# Revit family: PC RCD
name_source: partatom
category: Attrezzature speciali
revit_build: Autodesk Revit 2016 (Build: 20150714_1515(x64)
units: mm (PartAtom-declared; Revit-internal decimal feet)

## family parameters
Basato su piano di lavoro = No
Condiviso = No
Punto di calcolo locali = No
Quota connettore circolare = Usa diametro
Sempre verticale = Sì
Taglio con vuoti quando caricato = No
Tipo di parte = Normale

## types (6) — shared parameters
230 Volt = No
400 Volt = Sì
Air gap = Sì
Capacity factor = 80.00%
Clearance = 430 mm
Electrical supply = 400 V
Height = 1460 mm  [stored 4.79003 ft]
Latent Heat = 3.12 kW
Length = 717 mm  [stored 2.35236 ft]
Output racks/h = 40
Overall size = 1970 mm  [stored 6.46325 ft]
Rack size = 500 x 500
Rinse water consumption = 2.5 L
Sensible Heat = 2.15 kW
Tank drain = 35 mm  [stored 0.114829 ft]
Water inlet = 1"
Width = 740 mm  [stored 2.42782 ft]

## per-type parameters (varying)
| type | Apparent power | Installed Load | Total absorption | Water softener |
| PC07 R | 6200 VA | 7.8 kW | 13 A | No |
| PC07 RA | 6200 VA | 7.8 kW | 13 A | Sì |
| PC09 R | 8080 VA | 10.1 kW | 15 A | No |
| PC09 RA | 8080 VA | 10.1 kW | 15 A | Sì |
| PC12 R | 8400 VA | 10.5 kW | 16 A | No |
| PC12 RA | 8400 VA | 10.5 kW | 16 A | Sì |

note: [stored X ft] marks values corroborated as IEEE doubles in the binary element streams (Revit-internal decimal feet)
